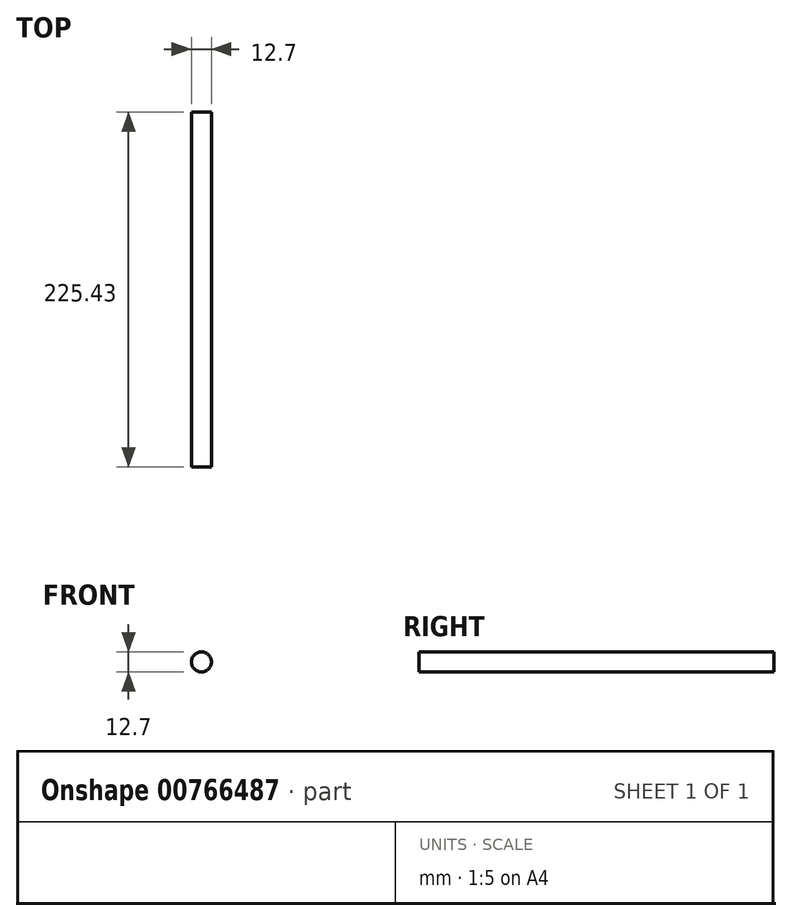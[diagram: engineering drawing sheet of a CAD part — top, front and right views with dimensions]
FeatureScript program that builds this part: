
annotation { "Feature Type Name" : "Feature", "Feature Type Description" : "" }
export const myFeature = defineFeature(function(context is Context, id is Id, definition is map)
    precondition{}
    {
        {
            var Q0;
            Q0=qCreatedBy(makeId("Front.planeOp"),FACE);
            var sketch = newSketch(context, id + "F0", { "sketchPlane" : qUnion([Q0])});
            skCircle(sketch, "E0", {"center": v(14.14, 42.56) * mm, "radius": 6.35 * mm});
            skSolve(sketch);
        }
        {
            var Q0;
            Q0=qSketchRegion(id+"F0",true);
            extrude(context, id + "F1", {"entities" : qUnion([Q0]), "oppositeDirection" : true, "depth" : 225.42 * mm, "offsetDistance" : 25.4 * mm});
        }
    });
